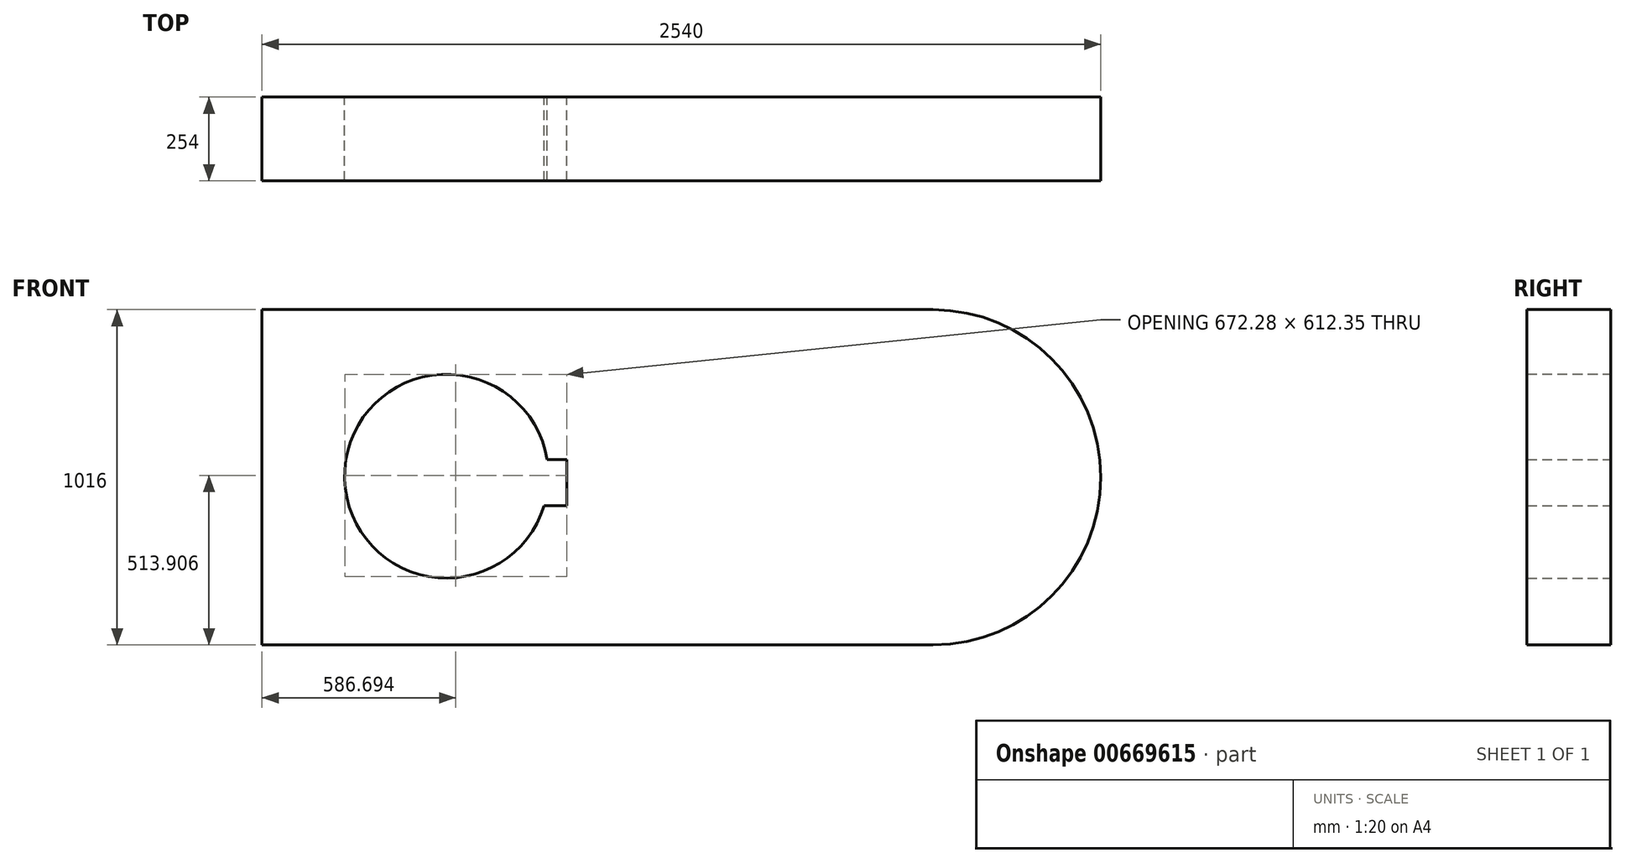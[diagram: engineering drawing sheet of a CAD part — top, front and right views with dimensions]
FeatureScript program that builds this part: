
annotation { "Feature Type Name" : "Feature", "Feature Type Description" : "" }
export const myFeature = defineFeature(function(context is Context, id is Id, definition is map)
    precondition{}
    {
        {
            var Q0;
            Q0=qCreatedBy(makeId("Front.planeOp"),FACE);
            var sketch = newSketch(context, id + "F0", { "sketchPlane" : qUnion([Q0])});
            skLineSegment(sketch, "E0.bottom", {"start": v(-529.74, -7.56) * mm, "end": v(-2561.74, -7.56) * mm});
            skLineSegment(sketch, "E0.top", {"start": v(-529.74, 1008.44) * mm, "end": v(-2561.74, 1008.44) * mm});
            skLineSegment(sketch, "E0.right", {"start": v(-2561.74, -7.56) * mm, "end": v(-2561.74, 1008.44) * mm});
            skArc(sketch, "E1", {"start": v(-529.74, -7.56) * mm, "mid": v(-21.74, 500.44) * mm, "end": v(-529.74, 1008.44) * mm});
            skArc(sketch, "E2", {"start": v(-1698.33, 554.55) * mm, "mid": v(-2311.18, 523.96) * mm, "end": v(-1707.34, 414.87) * mm});
            skLineSegment(sketch, "E3.bottom", {"start": v(-1638.9, 554.55) * mm, "end": v(-1698.33, 554.55) * mm});
            skLineSegment(sketch, "E3.top", {"start": v(-1638.9, 414.87) * mm, "end": v(-1707.34, 414.87) * mm});
            skLineSegment(sketch, "E3.left", {"start": v(-1638.9, 554.55) * mm, "end": v(-1638.9, 414.87) * mm});
            skPoint(sketch, "E3.middle", {"position": v(-1694.78, 484.71) * mm});
            skPoint(sketch, "E4.orphan", {"position": v(-1750.65, 414.87) * mm});
            skPoint(sketch, "E5.orphan", {"position": v(-1750.65, 554.55) * mm});
            skSolve(sketch);
        }
        {
            var Q0;
            Q0=makeQuery(id+"F0.imprint","IMPRINT",FACE,{"disambiguationData":[TD([[makeQuery(id+"F0.imprint","IMPRINT",EDGE,{"derivedFrom":sQuery(id+"F0.wireOp",EDGE,"E0.bottom")}),-1.0]])]});
            extrude(context, id + "F1", {"entities" : qUnion([Q0]), "depth" : 254 * mm, "offsetDistance" : 25.4 * mm});
        }
    });
